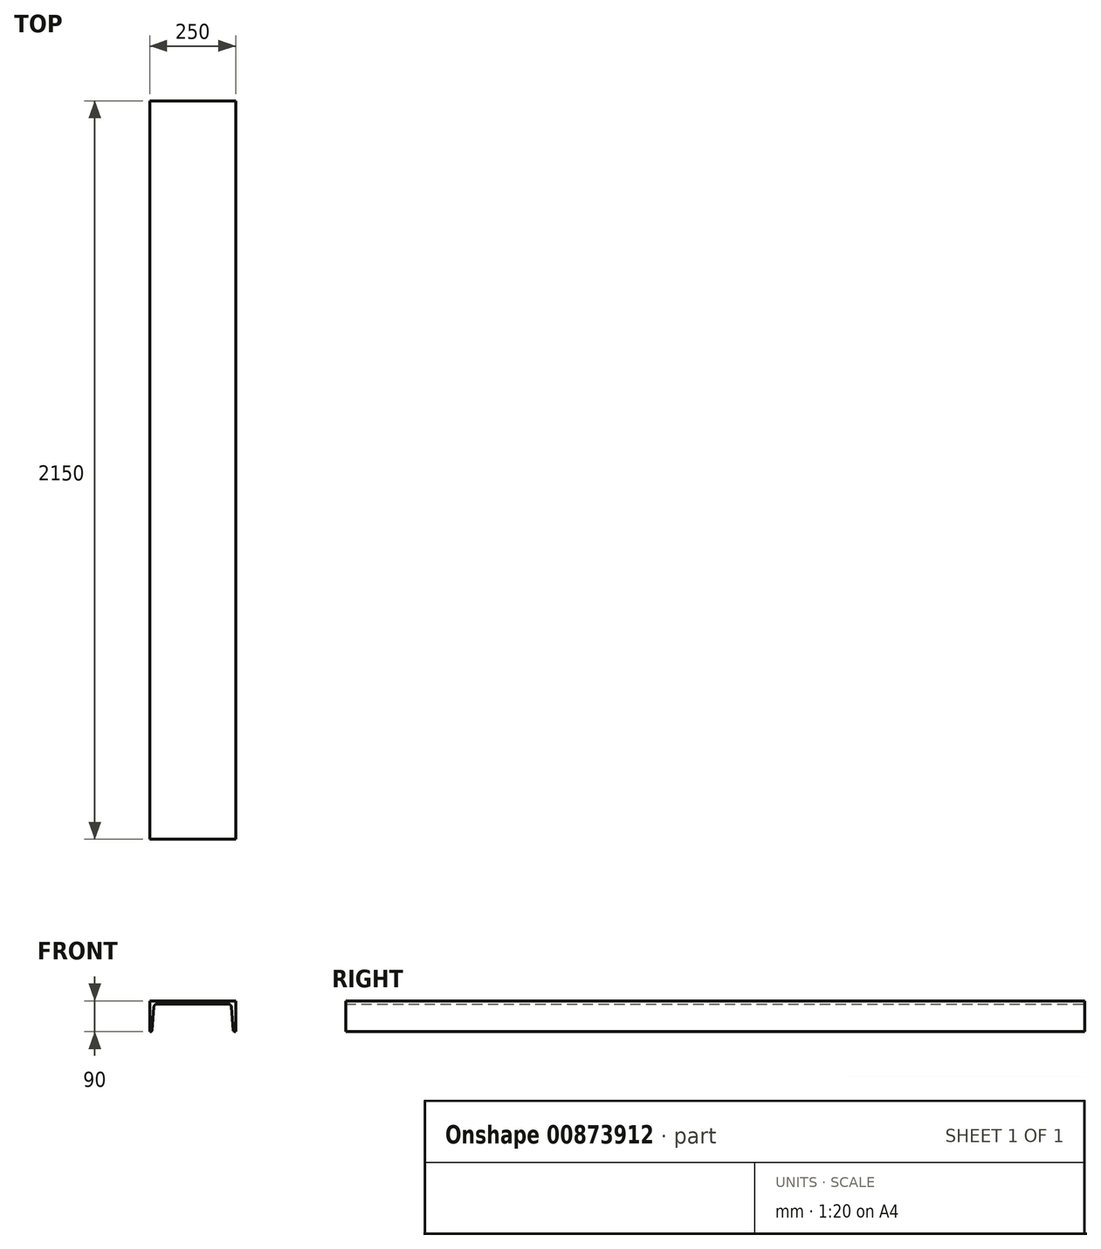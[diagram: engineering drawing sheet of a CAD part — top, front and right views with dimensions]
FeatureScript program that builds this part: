
annotation { "Feature Type Name" : "Feature", "Feature Type Description" : "" }
export const myFeature = defineFeature(function(context is Context, id is Id, definition is map)
    precondition{}
    {
        {
            var Q0;
            Q0=qCreatedBy(makeId("Front.planeOp"),FACE);
            var sketch = newSketch(context, id + "F0", { "sketchPlane" : qUnion([Q0])});
            skLineSegment(sketch, "E0.bottom", {"start": v(125, 45) * mm, "end": v(-125, 45) * mm});
            skLineSegment(sketch, "E0.top", {"start": v(125, -45) * mm, "end": v(123.11, -45) * mm});
            skLineSegment(sketch, "E0.left", {"start": v(125, 45) * mm, "end": v(125, -45) * mm});
            skLineSegment(sketch, "E0.right", {"start": v(-125, 45) * mm, "end": v(-125, -45) * mm});
            skPoint(sketch, "E0.middle", {"position": v(0, 0) * mm});
            skLineSegment(sketch, "E1.0", {"start": v(102.77, 36) * mm, "end": v(-102.77, 36) * mm});
            skLineSegment(sketch, "E2.trimOffspring", {"start": v(-123.11, -45) * mm, "end": v(-125, -45) * mm});
            skLineSegment(sketch, "E3", {"start": v(-112.74, 26.8) * mm, "end": v(-118.13, -40.4) * mm});
            skLineSegment(sketch, "E4", {"start": v(112.74, 26.8) * mm, "end": v(118.13, -40.4) * mm});
            skPoint(sketch, "E5.visualSharp", {"position": v(-118.5, -45) * mm});
            skArc(sketch, "E5.filletArc", {"start": v(-123.11, -45) * mm, "mid": v(-119.72, -43.67) * mm, "end": v(-118.13, -40.4) * mm});
            skPoint(sketch, "E6.visualSharp", {"position": v(118.5, -45) * mm});
            skArc(sketch, "E6.filletArc", {"start": v(118.13, -40.4) * mm, "mid": v(119.72, -43.67) * mm, "end": v(123.11, -45) * mm});
            skPoint(sketch, "E7.visualSharp", {"position": v(-112, 36) * mm});
            skArc(sketch, "E7.filletArc", {"start": v(-102.77, 36) * mm, "mid": v(-109.55, 33.35) * mm, "end": v(-112.74, 26.8) * mm});
            skPoint(sketch, "E8.visualSharp", {"position": v(112, 36) * mm});
            skArc(sketch, "E8.filletArc", {"start": v(112.74, 26.8) * mm, "mid": v(109.55, 33.35) * mm, "end": v(102.77, 36) * mm});
            skSolve(sketch);
        }
        {
            var Q0;
            Q0=makeQuery(id+"F0.imprint","IMPRINT",FACE,{"disambiguationData":[TD([[makeQuery(id+"F0.imprint","IMPRINT",EDGE,{"derivedFrom":sQuery(id+"F0.wireOp",EDGE,"E0.bottom")}),1.0]])]});
            extrude(context, id + "F1", {"entities" : qUnion([Q0]), "depth" : 2150 * mm, "offsetDistance" : 25 * mm, "symmetric" : true});
        }
    });
